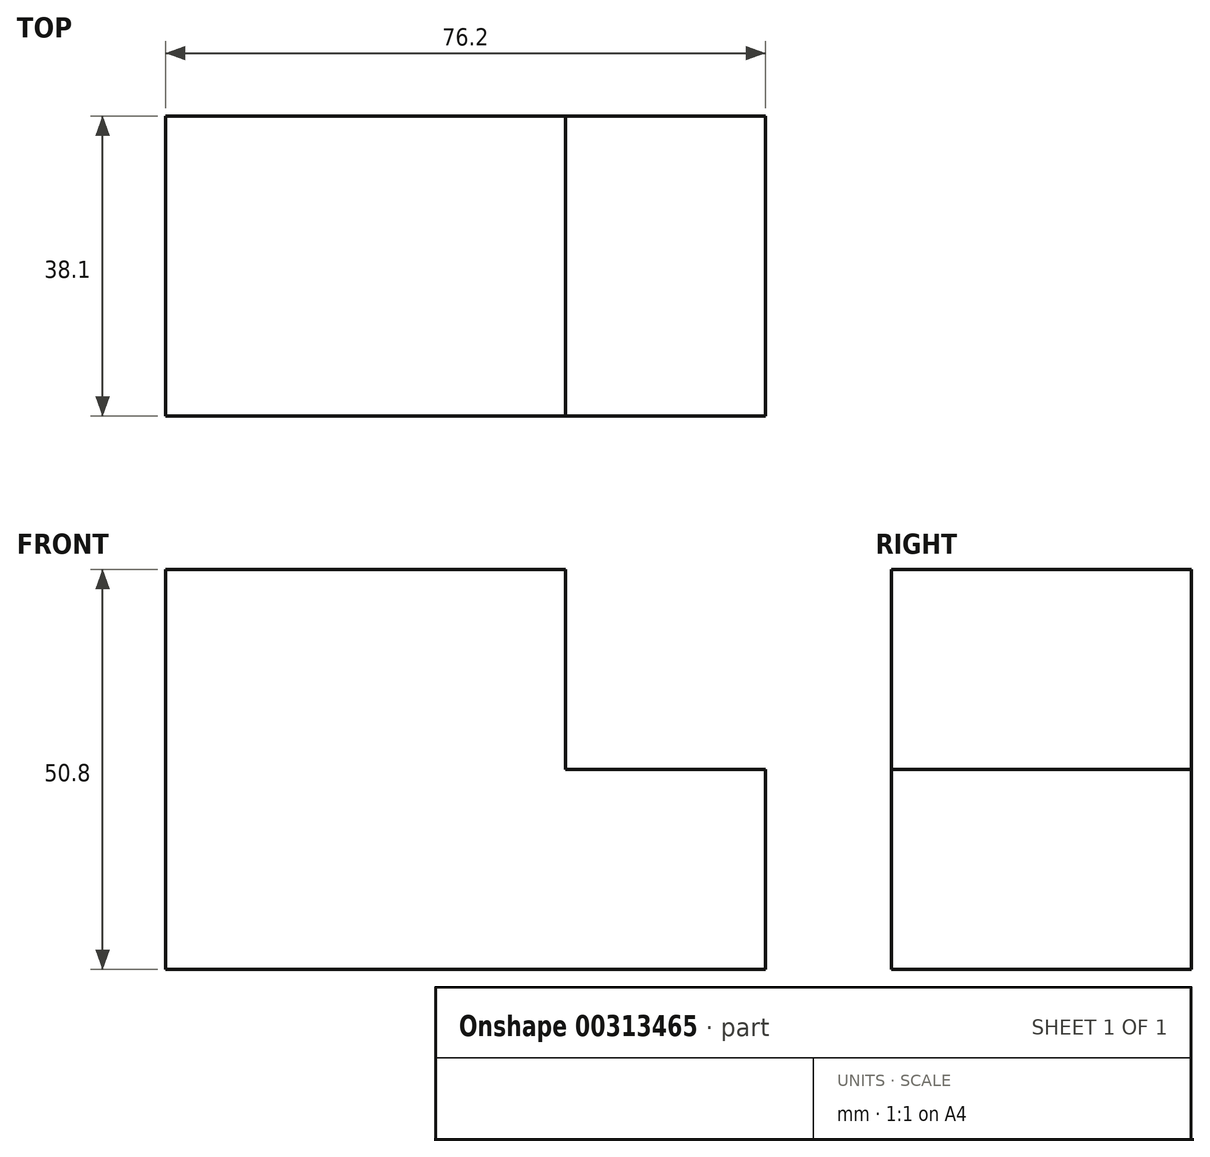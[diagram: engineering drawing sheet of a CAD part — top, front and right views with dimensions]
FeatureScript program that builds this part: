
annotation { "Feature Type Name" : "Feature", "Feature Type Description" : "" }
export const myFeature = defineFeature(function(context is Context, id is Id, definition is map)
    precondition{}
    {
        {
            var Q0;
            Q0=qCreatedBy(makeId("Front.planeOp"),FACE);
            var sketch = newSketch(context, id + "F0", { "sketchPlane" : qUnion([Q0])});
            skLineSegment(sketch, "E0", {"start": v(-37.38, -24.9) * mm, "end": v(38.82, -24.9) * mm});
            skLineSegment(sketch, "E1", {"start": v(38.82, -24.9) * mm, "end": v(38.82, 0.5) * mm});
            skLineSegment(sketch, "E2", {"start": v(38.82, 0.5) * mm, "end": v(13.42, 0.5) * mm});
            skLineSegment(sketch, "E3", {"start": v(13.42, 0.5) * mm, "end": v(13.42, 25.9) * mm});
            skLineSegment(sketch, "E4", {"start": v(13.42, 25.9) * mm, "end": v(-37.38, 25.9) * mm});
            skLineSegment(sketch, "E5", {"start": v(-37.38, 25.9) * mm, "end": v(-37.38, -24.9) * mm});
            skSolve(sketch);
        }
        {
            var Q0;
            Q0=makeQuery(id+"F0.imprint","IMPRINT",FACE,{"disambiguationData":[TD([[makeQuery(id+"F0.imprint","IMPRINT",EDGE,{"derivedFrom":sQuery(id+"F0.wireOp",EDGE,"E0")}),1.0]])]});
            extrude(context, id + "F1", {"entities" : qUnion([Q0]), "depth" : 38.1 * mm});
        }
    });
